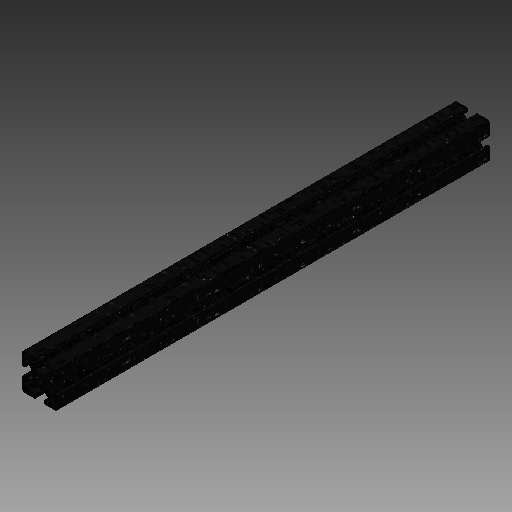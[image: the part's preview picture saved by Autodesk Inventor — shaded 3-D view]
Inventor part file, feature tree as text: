
AUTODESK INVENTOR PART (.ipt)
format: ipt  version: 2019 (Build 230136000, 136)  size: 261,120 bytes
history: native  units: in
note: dims shown in document units (in); Inventor stores cm internally (conversion verified against a paired STEP export)
features: extrude x1, sketch x1
ambient origin geometry x8: Origin, YZ Plane, XZ Plane, XY Plane, X Axis, Y Axis, Z Axis, Center Point
bodies: Solid1 (feature_tree)
feature tree (2):
  extrude  "Extrusion1"  [1 undecoded]
  sketch  "Sketch1"  dims[d0=18.0in d1=0.0in]
note: 1 required parameter value undecoded (feature->parameter linkage not recoverable at this tier; creation-order binding heuristic only, values carry confidence <= 0.55)
